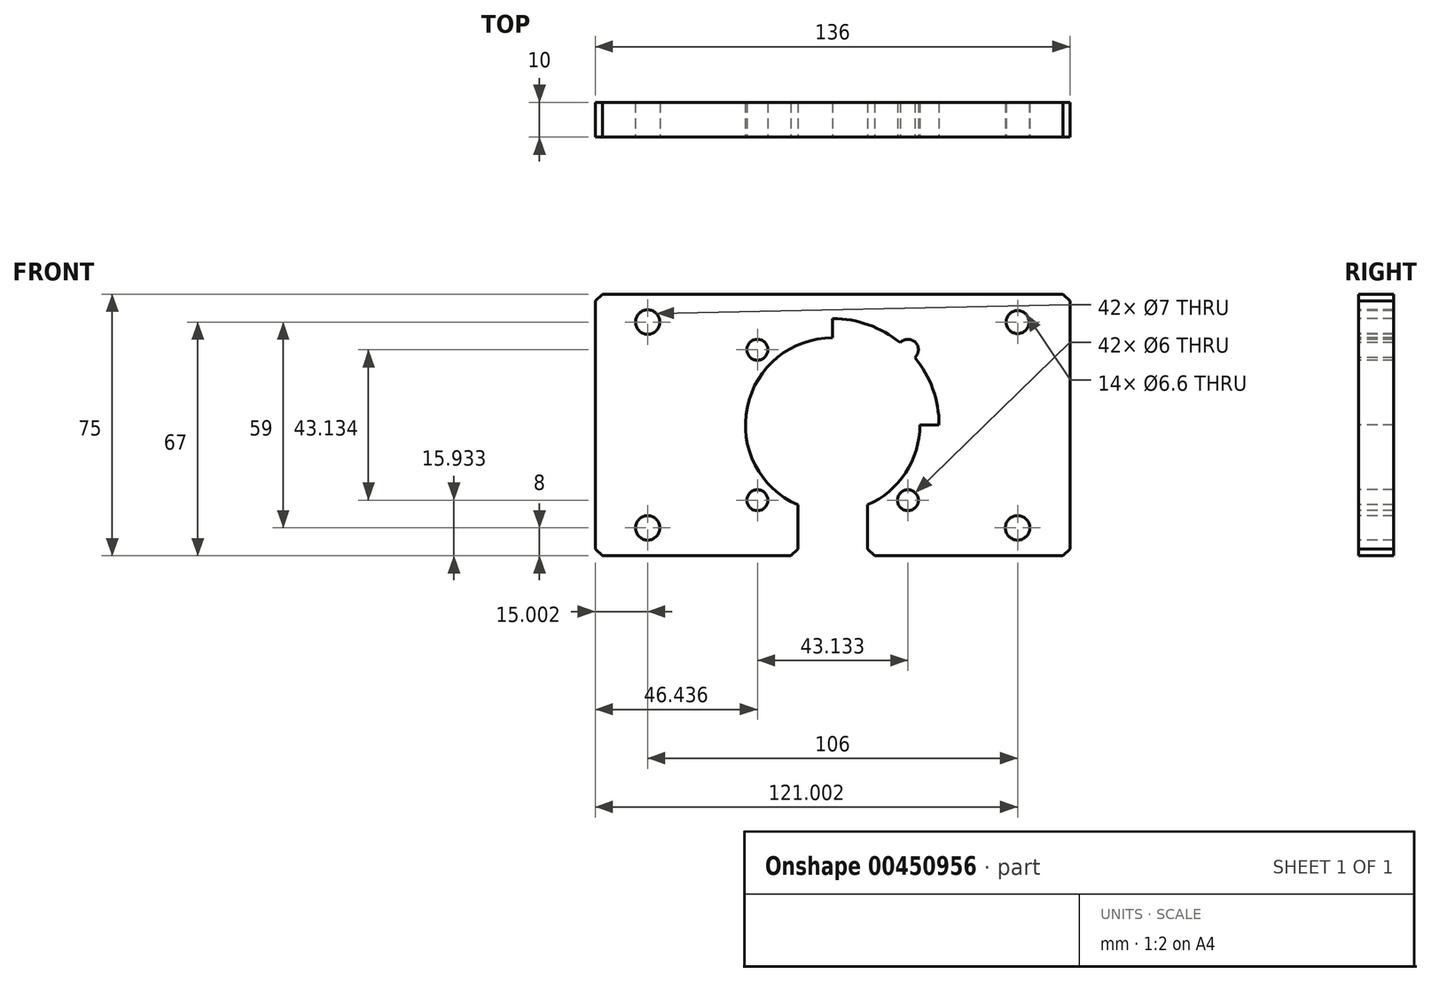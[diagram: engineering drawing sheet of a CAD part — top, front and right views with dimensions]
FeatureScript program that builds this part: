
annotation { "Feature Type Name" : "Feature", "Feature Type Description" : "" }
export const myFeature = defineFeature(function(context is Context, id is Id, definition is map)
    precondition{}
    {
        {
            var Q0;
            Q0=qCreatedBy(makeId("Front.planeOp"),FACE);
            var sketch = newSketch(context, id + "F0", { "sketchPlane" : qUnion([Q0])});
            skLineSegment(sketch, "E0", {"start": v(122.94, 44.71) * mm, "end": v(132.94, 44.71) * mm});
            skLineSegment(sketch, "E1", {"start": v(122.94, -30.29) * mm, "end": v(132.94, -30.29) * mm});
            skLineSegment(sketch, "E2", {"start": v(132.94, 44.71) * mm, "end": v(132.94, -30.29) * mm});
            skLineSegment(sketch, "E3", {"start": v(122.94, -30.29) * mm, "end": v(122.94, 44.71) * mm});
            skLineSegment(sketch, "E4", {"start": v(25.46, -30.29) * mm, "end": v(-28.54, -30.29) * mm});
            skLineSegment(sketch, "E5", {"start": v(27.46, -28.29) * mm, "end": v(25.46, -30.29) * mm});
            skLineSegment(sketch, "E6", {"start": v(25.46, 44.71) * mm, "end": v(-106.54, 44.71) * mm});
            skLineSegment(sketch, "E7", {"start": v(27.46, 42.71) * mm, "end": v(25.46, 44.71) * mm});
            skLineSegment(sketch, "E8", {"start": v(27.46, 42.71) * mm, "end": v(27.46, -28.29) * mm});
            skLineSegment(sketch, "E9", {"start": v(-108.54, 42.71) * mm, "end": v(-108.54, -28.29) * mm});
            skLineSegment(sketch, "E10", {"start": v(-106.54, 44.71) * mm, "end": v(-108.54, 42.71) * mm});
            skLineSegment(sketch, "E11", {"start": v(-106.54, -30.29) * mm, "end": v(-108.54, -28.29) * mm});
            skArc(sketch, "E12", {"start": v(-30.54, -15.7) * mm, "mid": v(-40.54, 32.21) * mm, "end": v(-50.54, -15.7) * mm});
            skLineSegment(sketch, "E13", {"start": v(-40.54, 39.71) * mm, "end": v(-40.54, -30.29) * mm});
            skLineSegment(sketch, "E14", {"start": v(-73.04, 7.21) * mm, "end": v(12.87, 7.21) * mm});
            skLineSegment(sketch, "E15", {"start": v(-30.54, -15.7) * mm, "end": v(-30.54, -28.29) * mm});
            skLineSegment(sketch, "E16", {"start": v(-50.54, -15.7) * mm, "end": v(-50.54, -28.29) * mm});
            skCircle(sketch, "E17", {"center": v(-40.54, 7.21) * mm, "radius": 30.5 * mm});
            skLineSegment(sketch, "E18", {"start": v(-15.79, 31.96) * mm, "end": v(-22.15, 25.6) * mm});
            skCircle(sketch, "E19", {"center": v(-18.97, 28.78) * mm, "radius": 3 * mm});
            skCircle(sketch, "E20", {"center": v(-18.97, 28.78) * mm, "radius": 2.46 * mm});
            skLineSegment(sketch, "E21", {"start": v(-65.29, 31.96) * mm, "end": v(-58.92, 25.6) * mm});
            skCircle(sketch, "E22", {"center": v(-62.1, 28.78) * mm, "radius": 3 * mm});
            skCircle(sketch, "E23", {"center": v(-62.1, 28.78) * mm, "radius": 2.46 * mm});
            skLineSegment(sketch, "E24", {"start": v(-65.29, -17.54) * mm, "end": v(-58.92, -11.17) * mm});
            skCircle(sketch, "E25", {"center": v(-62.1, -14.36) * mm, "radius": 3 * mm});
            skCircle(sketch, "E26", {"center": v(-62.1, -14.36) * mm, "radius": 2.46 * mm});
            skLineSegment(sketch, "E27", {"start": v(-15.79, -17.54) * mm, "end": v(-22.15, -11.17) * mm});
            skCircle(sketch, "E28", {"center": v(-18.97, -14.36) * mm, "radius": 3 * mm});
            skCircle(sketch, "E29", {"center": v(-18.97, -14.36) * mm, "radius": 2.46 * mm});
            skLineSegment(sketch, "E30", {"start": v(7.91, 36.71) * mm, "end": v(17.01, 36.71) * mm});
            skLineSegment(sketch, "E31", {"start": v(12.46, 32.16) * mm, "end": v(12.46, 41.26) * mm});
            skCircle(sketch, "E32", {"center": v(12.46, -22.29) * mm, "radius": 3.5 * mm});
            skCircle(sketch, "E33", {"center": v(-93.54, -22.29) * mm, "radius": 3.5 * mm});
            skCircle(sketch, "E34", {"center": v(-93.54, 36.71) * mm, "radius": 3.5 * mm});
            skLineSegment(sketch, "E35", {"start": v(7.91, -22.29) * mm, "end": v(17.01, -22.29) * mm});
            skLineSegment(sketch, "E36", {"start": v(12.46, -26.84) * mm, "end": v(12.46, -17.74) * mm});
            skLineSegment(sketch, "E37", {"start": v(-88.99, -22.29) * mm, "end": v(-98.09, -22.29) * mm});
            skLineSegment(sketch, "E38", {"start": v(-93.54, -17.74) * mm, "end": v(-93.54, -26.84) * mm});
            skLineSegment(sketch, "E39", {"start": v(-93.54, 32.16) * mm, "end": v(-93.54, 41.26) * mm});
            skLineSegment(sketch, "E40", {"start": v(-88.99, 36.71) * mm, "end": v(-98.09, 36.71) * mm});
            skLineSegment(sketch, "E41", {"start": v(-52.54, -30.29) * mm, "end": v(-106.54, -30.29) * mm});
            skLineSegment(sketch, "E42", {"start": v(-28.54, -30.29) * mm, "end": v(-30.54, -28.29) * mm});
            skLineSegment(sketch, "E43", {"start": v(-50.54, -28.29) * mm, "end": v(-52.54, -30.29) * mm});
            skCircle(sketch, "E44", {"center": v(12.46, 36.71) * mm, "radius": 3.3 * mm});
            skSolve(sketch);
        }
        {
            var Q0;
            Q0=makeQuery(id+"F0.imprint","IMPRINT",FACE,{"disambiguationData":[TD([[makeQuery(id+"F0.imprint","IMPRINT",EDGE,{"derivedFrom":sQuery(id+"F0.wireOp",EDGE,"E4")}),-1.0]])]});
            var Q1;
            {var subQ6=sQuery(id+"F0.wireOp",EDGE,"E14");var subQ8=sQuery(id+"F0.wireOp",EDGE,"E12");var subQ9=makeQuery(id+"F0.imprint","INTERSECT",VERTEX,{"disambiguationData":[OD(0.0)],"derivedFrom":[subQ8,subQ6]});Q1=makeQuery(id+"F0.imprint","IMPRINT",FACE,{"disambiguationData":[TD([[makeQuery(id+"F0.imprint","IMPRINT",EDGE,{"disambiguationData":[TD([[subQ9,-1.0]])],"derivedFrom":subQ8}),-1.0]])]});}
            var Q2;
            {var subQ5=sQuery(id+"F0.wireOp",EDGE,"E12");var subQ7=sQuery(id+"F0.wireOp",EDGE,"E13");var subQ9=makeQuery(id+"F0.imprint","INTERSECT",VERTEX,{"derivedFrom":[subQ5,subQ7]});Q2=makeQuery(id+"F0.imprint","IMPRINT",FACE,{"disambiguationData":[TD([[makeQuery(id+"F0.imprint","IMPRINT",EDGE,{"disambiguationData":[TD([[subQ9,-1.0]])],"derivedFrom":subQ5}),-1.0]])]});}
            var Q3;
            {var subQ3=sQuery(id+"F0.wireOp",EDGE,"E12");var subQ5=sQuery(id+"F0.wireOp",EDGE,"E16");var subQ9=makeQuery(id+"F0.imprint","INTERSECT",VERTEX,{"derivedFrom":[subQ3,subQ5]});Q3=makeQuery(id+"F0.imprint","IMPRINT",FACE,{"disambiguationData":[TD([[makeQuery(id+"F0.imprint","IMPRINT",EDGE,{"disambiguationData":[TD([[subQ9,1.0]])],"derivedFrom":subQ3}),-1.0]])]});}
            var Q4;
            {var subQ0=sQuery(id+"F0.wireOp",EDGE,"E15");var subQ1=sQuery(id+"F0.wireOp",EDGE,"E12");var subQ2=makeQuery(id+"F0.imprint","INTERSECT",VERTEX,{"derivedFrom":[subQ1,subQ0]});Q4=makeQuery(id+"F0.imprint","IMPRINT",FACE,{"disambiguationData":[TD([[makeQuery(id+"F0.imprint","IMPRINT",EDGE,{"disambiguationData":[TD([[subQ2,-1.0]])],"derivedFrom":subQ1}),-1.0]])]});}
            extrude(context, id + "F1", {"entities" : qUnion([Q0, Q1, Q2, Q3, Q4]), "oppositeDirection" : true, "depth" : 10 * mm});
        }
    });
